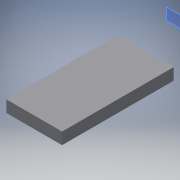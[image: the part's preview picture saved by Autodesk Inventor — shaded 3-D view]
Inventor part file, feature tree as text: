
AUTODESK INVENTOR PART (.ipt)
format: ipt  version: 2017 (Build 210142000, 142)  size: 88,576 bytes
history: native  units: in
note: dims shown in document units (in); Inventor stores cm internally (conversion verified against a paired STEP export)
features: extrude x1, sketch x1
ambient origin geometry x8: Origin, YZ Plane, XZ Plane, XY Plane, X Axis, Y Axis, Z Axis, Center Point
bodies: Solid1 (feature_tree)
feature tree (2):
  extrude  "Extrusion1"  Depth=78.7402in
  sketch  "Sketch1"  dims[d0=39.3701in d1=78.7402in d2=8.3in d3=0.0in]
